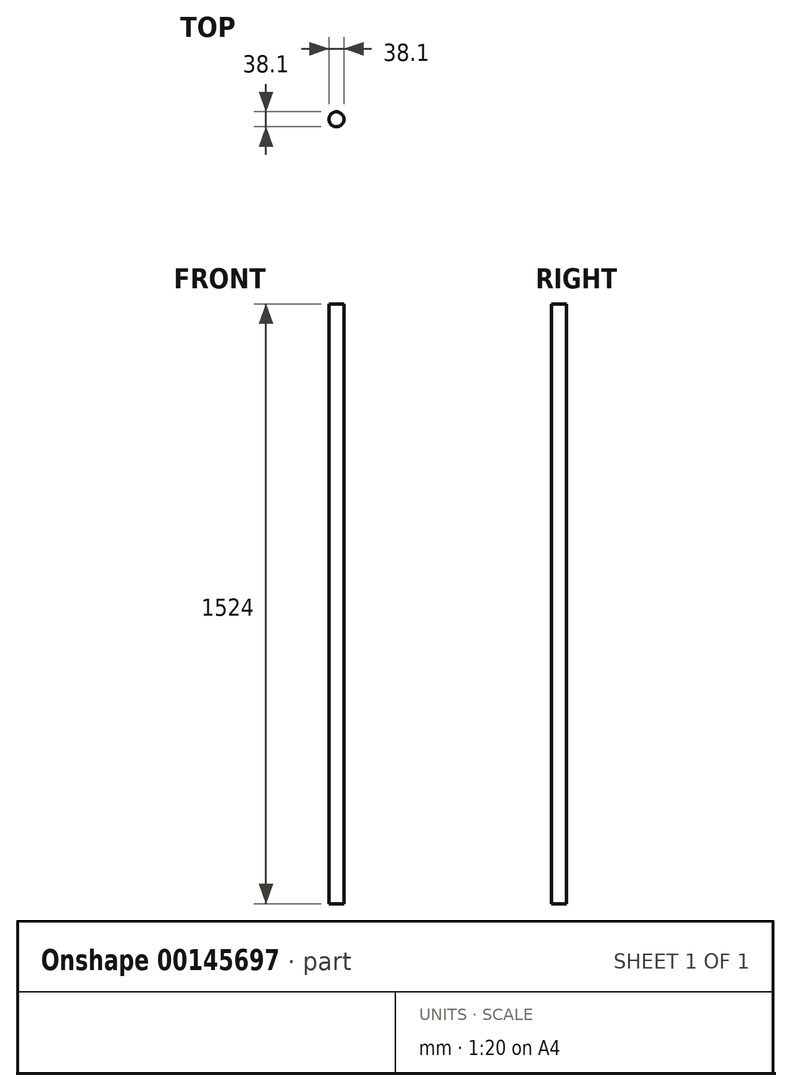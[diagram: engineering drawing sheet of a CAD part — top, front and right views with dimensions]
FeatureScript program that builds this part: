
annotation { "Feature Type Name" : "Feature", "Feature Type Description" : "" }
export const myFeature = defineFeature(function(context is Context, id is Id, definition is map)
    precondition{}
    {
        {
            var Q0;
            Q0=qCreatedBy(makeId("Top.planeOp"),FACE);
            var sketch = newSketch(context, id + "F0", { "sketchPlane" : qUnion([Q0])});
            skCircle(sketch, "E0", {"center": v(0, 0) * mm, "radius": 19.05 * mm});
            skSolve(sketch);
        }
        {
            var Q0;
            Q0 = qSketchRegion(id + "F0", true);
            extrude(context, id + "F1", {"entities" : qUnion([Q0]), "depth" : 1524 * mm});
        }
    });
